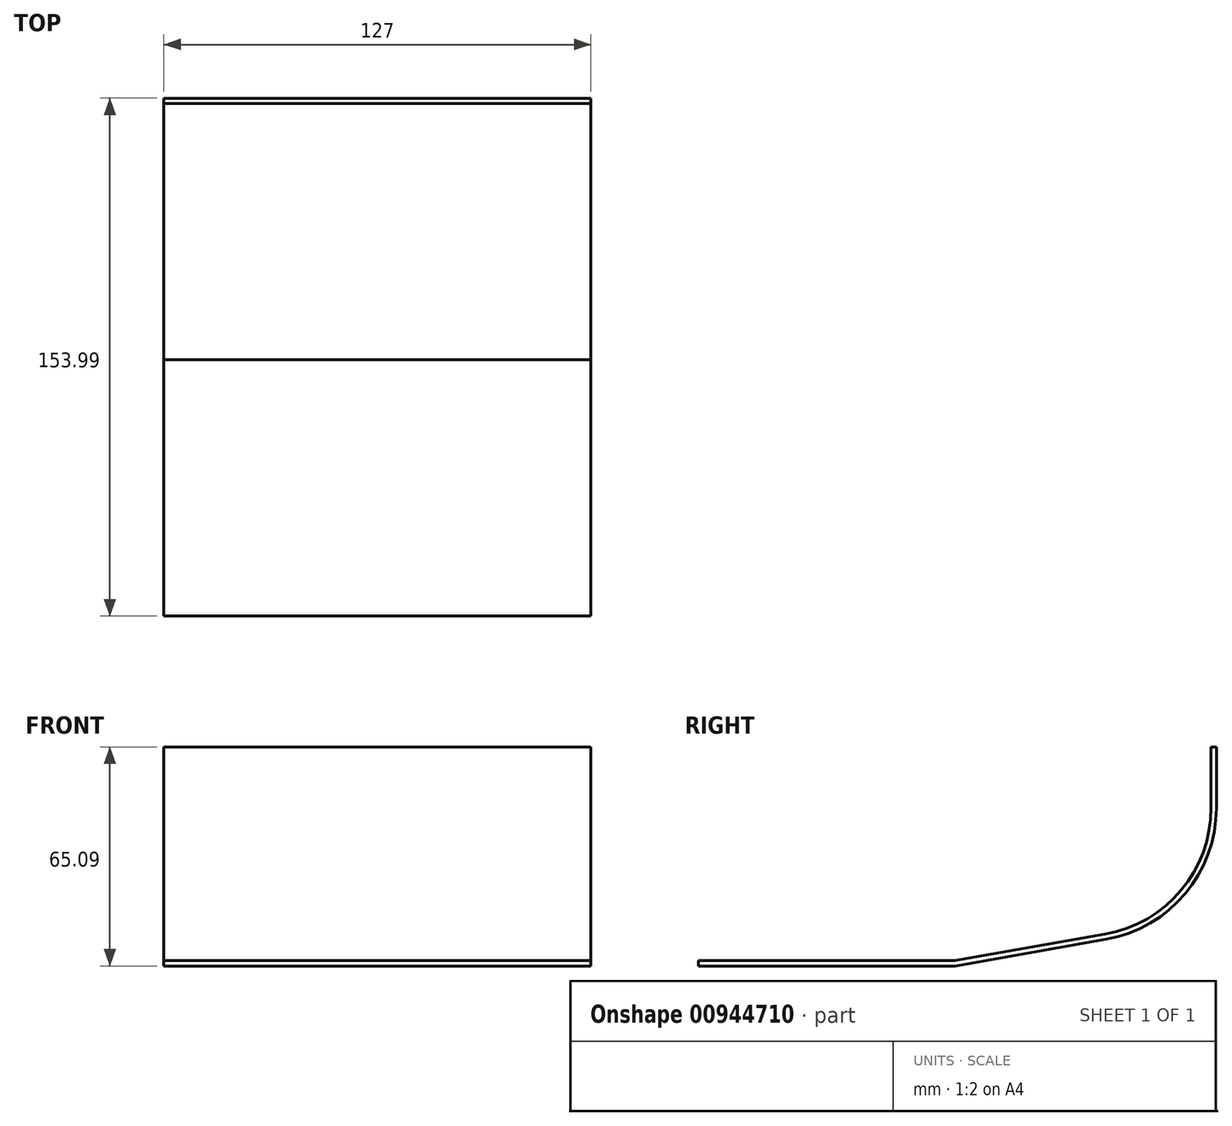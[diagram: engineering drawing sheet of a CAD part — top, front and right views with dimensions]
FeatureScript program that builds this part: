
annotation { "Feature Type Name" : "Feature", "Feature Type Description" : "" }
export const myFeature = defineFeature(function(context is Context, id is Id, definition is map)
    precondition{}
    {
        {
            var Q0;
            Q0=qCreatedBy(makeId("Right.planeOp"),FACE);
            var sketch = newSketch(context, id + "F0", { "sketchPlane" : qUnion([Q0])});
            skLineSegment(sketch, "E0.bottom", {"start": v(0, 0) * mm, "end": v(152.4, 0) * mm});
            skLineSegment(sketch, "E0.top", {"start": v(0, 63.5) * mm, "end": v(153.99, 63.5) * mm});
            skLineSegment(sketch, "E0.left", {"start": v(0, -1.59) * mm, "end": v(0, 63.5) * mm});
            skLineSegment(sketch, "E0.right", {"start": v(152.4, 45.4) * mm, "end": v(152.4, 63.5) * mm});
            skLineSegment(sketch, "E1", {"start": v(0, 0) * mm, "end": v(152.4, 63.5) * mm});
            skLineSegment(sketch, "E2", {"start": v(76.2, 0) * mm, "end": v(120.92, 7.88) * mm});
            skArc(sketch, "E3.filletArc", {"start": v(120.92, 7.88) * mm, "mid": v(143.49, 20.92) * mm, "end": v(152.4, 45.4) * mm});
            skLineSegment(sketch, "E4.0", {"start": v(153.99, 45.4) * mm, "end": v(153.99, 63.5) * mm});
            skArc(sketch, "E4.1", {"start": v(121.2, 6.32) * mm, "mid": v(144.7, 19.9) * mm, "end": v(153.99, 45.4) * mm});
            skLineSegment(sketch, "E4.2", {"start": v(76.34, -1.59) * mm, "end": v(121.2, 6.32) * mm});
            skLineSegment(sketch, "E5.0", {"start": v(0, -1.59) * mm, "end": v(152.4, -1.59) * mm});
            skSolve(sketch);
        }
        {
            var Q0;
            {var subQ1=sQuery(id+"F0.wireOp",EDGE,"E0.right");Q0=makeQuery(id+"F0.imprint","IMPRINT",FACE,{"disambiguationData":[TD([[makeQuery(id+"F0.imprint","IMPRINT",EDGE,{"derivedFrom":subQ1}),-1.0]])]});}
            var Q1;
            {var subQ3=sQuery(id+"F0.wireOp",EDGE,"E0.bottom");var subQ5=makeQuery(id+"F0.imprint","INTERSECT",VERTEX,{"derivedFrom":[subQ3,sQuery(id+"F0.wireOp",EDGE,"E2")]});Q1=makeQuery(id+"F0.imprint","IMPRINT",FACE,{"disambiguationData":[TD([[makeQuery(id+"F0.imprint","IMPRINT",EDGE,{"disambiguationData":[TD([[subQ5,-1.0]])],"derivedFrom":subQ3}),-1.0]])]});}
            extrude(context, id + "F1", {"entities" : qUnion([Q0, Q1]), "depth" : 127 * mm, "offsetDistance" : 25.4 * mm});
        }
    });
